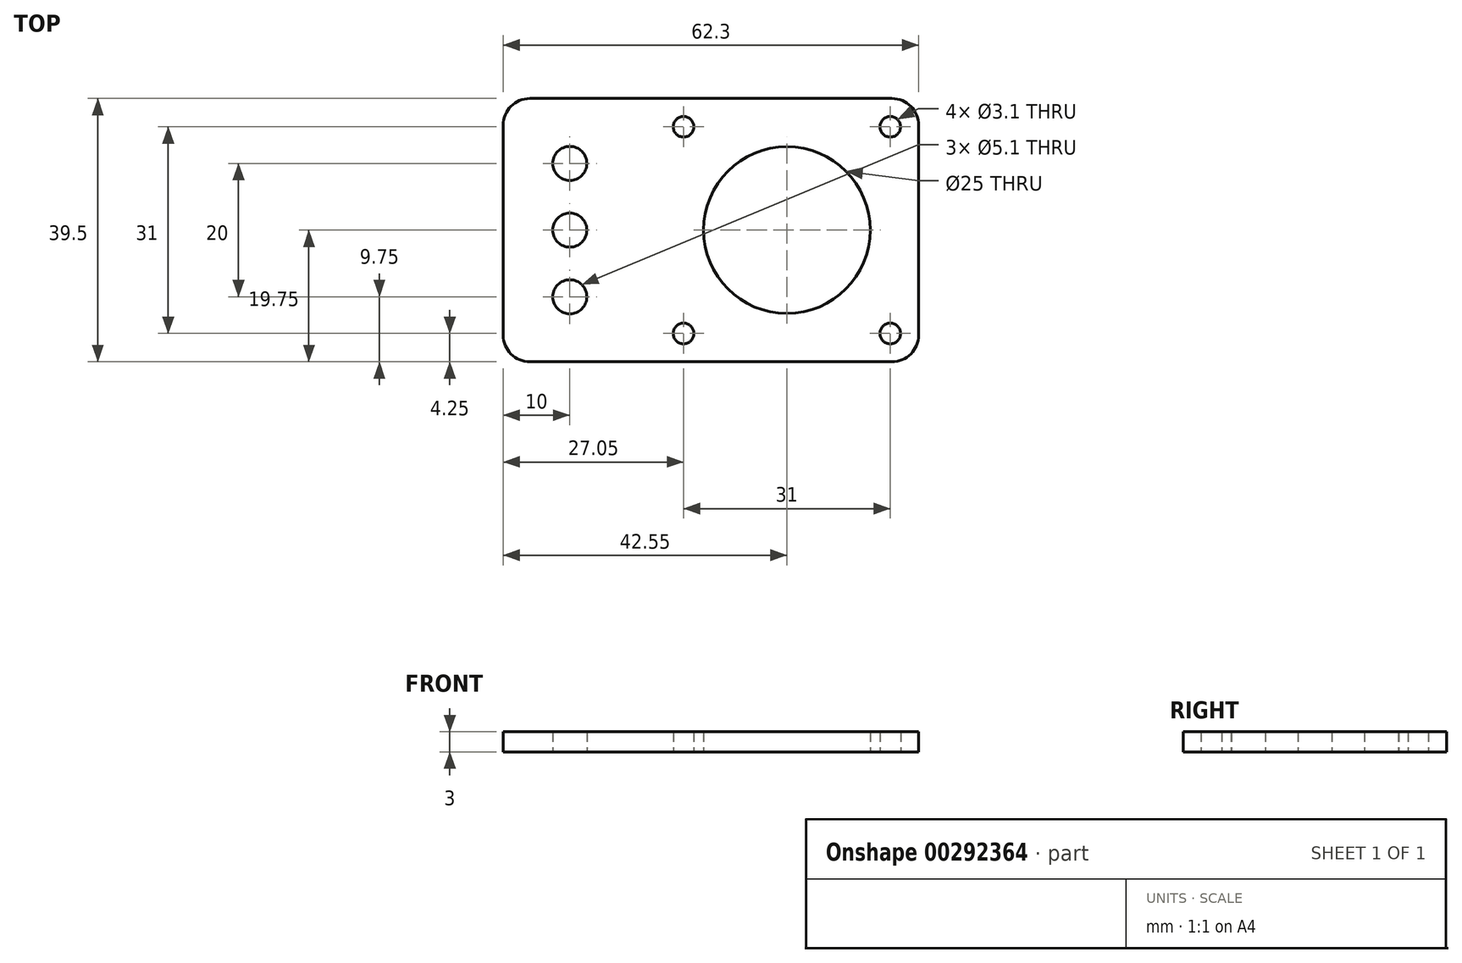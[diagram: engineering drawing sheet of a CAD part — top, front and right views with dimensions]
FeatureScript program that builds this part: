
annotation { "Feature Type Name" : "Feature", "Feature Type Description" : "" }
export const myFeature = defineFeature(function(context is Context, id is Id, definition is map)
    precondition{}
    {
        {
            var Q0;
            Q0=qCreatedBy(makeId("Top.planeOp"),FACE);
            var sketch = newSketch(context, id + "F0", { "sketchPlane" : qUnion([Q0])});
            skCircle(sketch, "E0", {"center": v(0, 0) * mm, "radius": 12.5 * mm});
            skLineSegment(sketch, "E1.rect.bottom", {"start": v(15.75, 19.75) * mm, "end": v(-38.55, 19.75) * mm});
            skLineSegment(sketch, "E1.rect.top", {"start": v(15.75, -19.75) * mm, "end": v(-38.55, -19.75) * mm});
            skLineSegment(sketch, "E1.rect.left", {"start": v(19.75, 15.75) * mm, "end": v(19.75, -15.75) * mm});
            skPoint(sketch, "E2.visualSharp", {"position": v(19.75, 19.75) * mm});
            skArc(sketch, "E2.filletArc", {"start": v(19.75, 15.75) * mm, "mid": v(18.58, 18.58) * mm, "end": v(15.75, 19.75) * mm});
            skPoint(sketch, "E3.visualSharp", {"position": v(19.75, -19.75) * mm});
            skArc(sketch, "E3.filletArc", {"start": v(15.75, -19.75) * mm, "mid": v(18.58, -18.58) * mm, "end": v(19.75, -15.75) * mm});
            skLineSegment(sketch, "E4", {"start": v(0, 0) * mm, "end": v(19.75, 0) * mm, "construction": true});
            skCircle(sketch, "E5", {"center": v(-15.5, 15.5) * mm, "radius": 1.55 * mm});
            skLineSegment(sketch, "E6", {"start": v(0, 19.75) * mm, "end": v(0, -19.75) * mm, "construction": true});
            skCircle(sketch, "E7.1.0", {"center": v(-15.5, -15.5) * mm, "radius": 1.55 * mm});
            skCircle(sketch, "E7.2.0", {"center": v(15.5, -15.5) * mm, "radius": 1.55 * mm});
            skCircle(sketch, "E7.3.0", {"center": v(15.5, 15.5) * mm, "radius": 1.55 * mm});
            skLineSegment(sketch, "E8", {"start": v(0, 0) * mm, "end": v(19.75, 19.75) * mm, "construction": true});
            skLineSegment(sketch, "E9", {"start": v(-32.55, 19.75) * mm, "end": v(-32.55, -19.75) * mm, "construction": true});
            skCircle(sketch, "E10", {"center": v(-32.55, 10) * mm, "radius": 2.55 * mm});
            skCircle(sketch, "E11", {"center": v(-32.55, 0) * mm, "radius": 2.55 * mm});
            skCircle(sketch, "E12.MirrorC", {"center": v(-32.55, -10) * mm, "radius": 2.55 * mm});
            skLineSegment(sketch, "E13", {"start": v(-42.55, 15.75) * mm, "end": v(-42.55, -15.75) * mm});
            skPoint(sketch, "E14.visualSharp", {"position": v(-42.55, 19.75) * mm});
            skArc(sketch, "E14.filletArc", {"start": v(-38.55, 19.75) * mm, "mid": v(-41.38, 18.58) * mm, "end": v(-42.55, 15.75) * mm});
            skPoint(sketch, "E15.visualSharp", {"position": v(-42.55, -19.75) * mm});
            skArc(sketch, "E15.filletArc", {"start": v(-42.55, -15.75) * mm, "mid": v(-41.38, -18.58) * mm, "end": v(-38.55, -19.75) * mm});
            skSolve(sketch);
        }
        {
            var Q0;
            Q0=makeQuery(id+"F0.imprint","IMPRINT",FACE,{"disambiguationData":[TD([[makeQuery(id+"F0.imprint","IMPRINT",EDGE,{"derivedFrom":sQuery(id+"F0.wireOp",EDGE,"E0")}),-1.0]])]});
            extrude(context, id + "F1", {"entities" : qUnion([Q0]), "depth" : 3 * mm});
        }
    });
